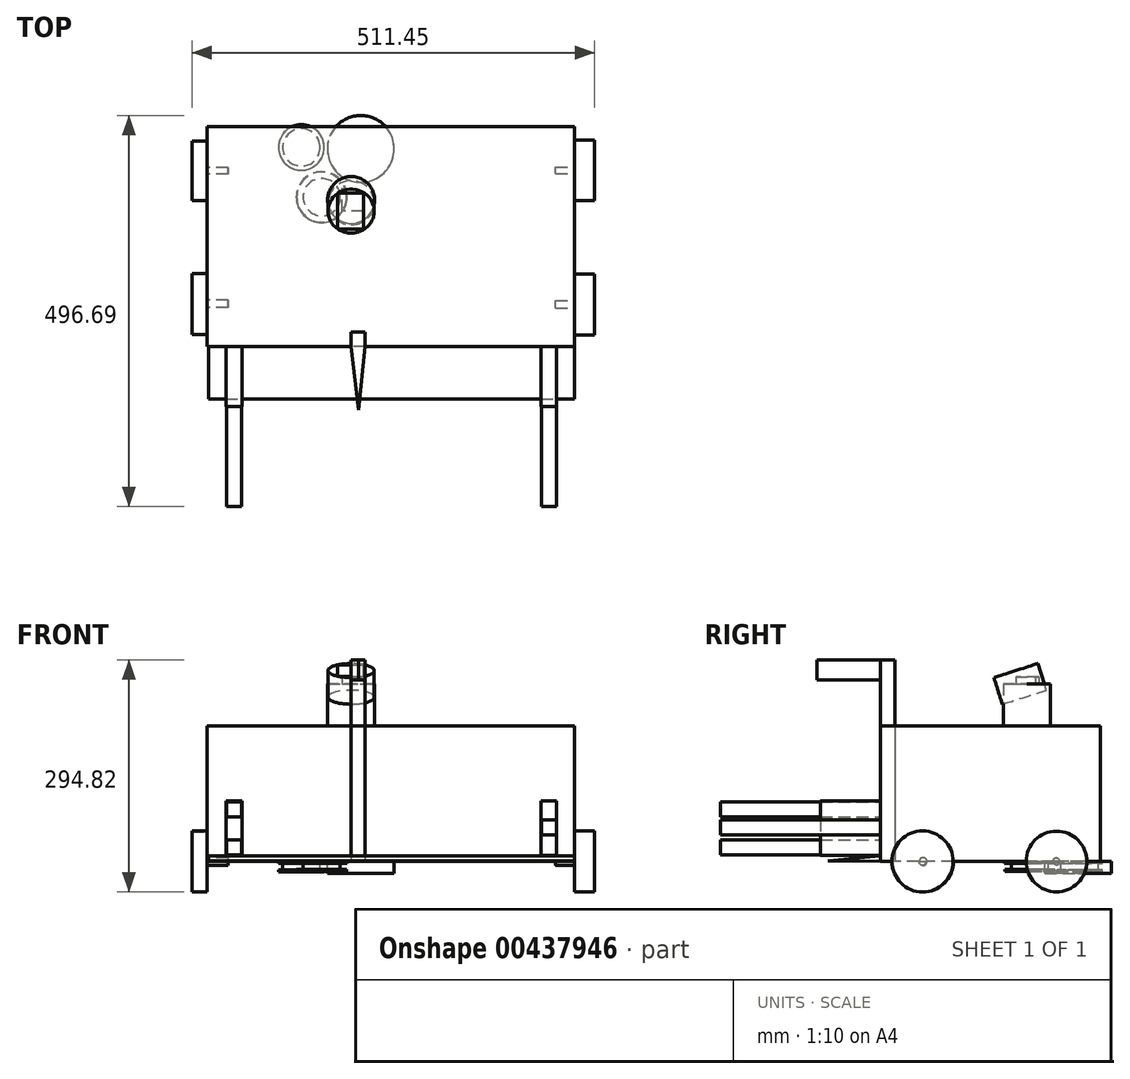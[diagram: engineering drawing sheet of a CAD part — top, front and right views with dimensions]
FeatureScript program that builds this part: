
annotation { "Feature Type Name" : "Feature", "Feature Type Description" : "" }
export const myFeature = defineFeature(function(context is Context, id is Id, definition is map)
    precondition{}
    {
        {
            var Q0;
            Q0=qCreatedBy(makeId("Front.planeOp"),FACE);
            var sketch = newSketch(context, id + "F0", { "sketchPlane" : qUnion([Q0])});
            skLineSegment(sketch, "E0.bottom", {"start": v(-158.36, 44.61) * mm, "end": v(-139.3, 44.61) * mm});
            skLineSegment(sketch, "E0.top", {"start": v(-158.36, 25.56) * mm, "end": v(-139.3, 25.56) * mm});
            skLineSegment(sketch, "E0.left", {"start": v(-158.36, 44.61) * mm, "end": v(-158.36, 25.56) * mm});
            skLineSegment(sketch, "E0.right", {"start": v(-139.3, 44.61) * mm, "end": v(-139.3, 25.56) * mm});
            skLineSegment(sketch, "E1.bottom", {"start": v(-158.13, -4.21) * mm, "end": v(-139.08, -4.21) * mm});
            skLineSegment(sketch, "E1.top", {"start": v(-158.13, -23.26) * mm, "end": v(-139.08, -23.26) * mm});
            skLineSegment(sketch, "E1.left", {"start": v(-158.13, -4.21) * mm, "end": v(-158.13, -23.26) * mm});
            skLineSegment(sketch, "E1.right", {"start": v(-139.08, -4.21) * mm, "end": v(-139.08, -23.26) * mm});
            skLineSegment(sketch, "E2.bottom", {"start": v(241.6, 21.7) * mm, "end": v(260.66, 21.7) * mm});
            skLineSegment(sketch, "E2.top", {"start": v(241.6, 2.65) * mm, "end": v(260.66, 2.65) * mm});
            skLineSegment(sketch, "E2.left", {"start": v(241.6, 21.7) * mm, "end": v(241.6, 2.65) * mm});
            skLineSegment(sketch, "E2.right", {"start": v(260.66, 21.7) * mm, "end": v(260.66, 2.65) * mm});
            skText(sketch, "E3", { "text": "carson anderson\n", "fontName": "OpenSans-Regular.ttf"});
            const initialGuessF0  = {"E3": [0.0572, 0.06518, 1, 0, 0.0084]};
            skSetInitialGuess(sketch, initialGuessF0);
            skSolve(sketch);
        }
        {
            var Q0;
            Q0=makeQuery(id+"F0.imprint","IMPRINT",FACE,{"disambiguationData":[TD([[makeQuery(id+"F0.imprint","IMPRINT",EDGE,{"derivedFrom":sQuery(id+"F0.wireOp",EDGE,"E0.bottom")}),-1.0]])]});
            var Q1;
            Q1=makeQuery(id+"F0.imprint","IMPRINT",FACE,{"disambiguationData":[TD([[makeQuery(id+"F0.imprint","IMPRINT",EDGE,{"derivedFrom":sQuery(id+"F0.wireOp",EDGE,"E1.bottom")}),-1.0]])]});
            var Q2;
            Q2=makeQuery(id+"F0.imprint","IMPRINT",FACE,{"disambiguationData":[TD([[makeQuery(id+"F0.imprint","IMPRINT",EDGE,{"derivedFrom":sQuery(id+"F0.wireOp",EDGE,"E2.bottom")}),-1.0]])]});
            extrude(context, id + "F1", {"entities" : qUnion([Q0, Q1, Q2]), "depth" : 203.2 * mm});
        }
        {
            var Q0;
            Q0=qCreatedBy(makeId("Front.planeOp"),FACE);
            var sketch = newSketch(context, id + "F2", { "sketchPlane" : qUnion([Q0])});
            skLineSegment(sketch, "E4.bottom", {"start": v(-138.56, 45.6) * mm, "end": v(-159.13, 45.6) * mm});
            skLineSegment(sketch, "E4.top", {"start": v(-138.56, -23.5) * mm, "end": v(-159.13, -23.5) * mm});
            skLineSegment(sketch, "E4.left", {"start": v(-138.56, 45.6) * mm, "end": v(-138.56, -23.5) * mm});
            skLineSegment(sketch, "E4.right", {"start": v(-159.13, 45.6) * mm, "end": v(-159.13, -23.5) * mm});
            skLineSegment(sketch, "E5.bottom", {"start": v(260.62, 45.42) * mm, "end": v(241.43, 45.42) * mm});
            skLineSegment(sketch, "E5.top", {"start": v(260.62, -23.5) * mm, "end": v(241.43, -23.5) * mm});
            skLineSegment(sketch, "E5.left", {"start": v(260.62, 45.42) * mm, "end": v(260.62, -23.5) * mm});
            skLineSegment(sketch, "E5.right", {"start": v(241.43, 45.42) * mm, "end": v(241.43, -23.5) * mm});
            skSolve(sketch);
        }
        {
            var Q0;
            Q0 = qSketchRegion(id + "F2", true);
            extrude(context, id + "F3", {"entities" : qUnion([Q0]), "depth" : 76.2 * mm});
        }
        {
            var Q0;
            Q0=qCreatedBy(makeId("Front.planeOp"),FACE);
            var sketch = newSketch(context, id + "F4", { "sketchPlane" : qUnion([Q0])});
            skLineSegment(sketch, "E6.bottom", {"start": v(283.8, -31.38) * mm, "end": v(-183.2, -31.38) * mm});
            skLineSegment(sketch, "E6.top", {"start": v(283.8, 140.95) * mm, "end": v(-183.2, 140.95) * mm});
            skLineSegment(sketch, "E6.left", {"start": v(283.8, -31.38) * mm, "end": v(283.8, 140.95) * mm});
            skLineSegment(sketch, "E6.right", {"start": v(-183.2, -31.38) * mm, "end": v(-183.2, 140.95) * mm});
            skSolve(sketch);
        }
        {
            var Q0;
            Q0 = qSketchRegion(id + "F4", true);
            extrude(context, id + "F5", {"entities" : qUnion([Q0]), "depth" : -279.4 * mm});
        }
        {
            var Q0;
            Q0=makeQuery(id+"F5.opExtrude","SWEPT_FACE",FACE,{"disambiguationData":[OSD([sQuery(id+"F4.wireOp",EDGE,"E6.right")])]});
            var sketch = newSketch(context, id + "F6", { "sketchPlane" : qUnion([Q0])});
            skCircle(sketch, "E7", {"center": v(-54.1, -31.38) * mm, "radius": 38.66 * mm});
            skCircle(sketch, "E8", {"center": v(-223.24, -31.38) * mm, "radius": 37.87 * mm});
            skSolve(sketch);
        }
        {
            var Q0;
            Q0 = qSketchRegion(id + "F6", true);
            extrude(context, id + "F7", {"entities" : qUnion([Q0]), "depth" : 19.05 * mm});
        }
        {
            var Q0;
            Q0=makeQuery(id+"F5.opExtrude","SWEPT_FACE",FACE,{"disambiguationData":[OSD([sQuery(id+"F4.wireOp",EDGE,"E6.right")])]});
            var sketch = newSketch(context, id + "F8", { "sketchPlane" : qUnion([Q0])});
            skCircle(sketch, "E9", {"center": v(-223.26, -31.38) * mm, "radius": 4.32 * mm});
            skCircle(sketch, "E10", {"center": v(-54.16, -31.38) * mm, "radius": 4.89 * mm});
            skSolve(sketch);
        }
        {
            var Q0;
            Q0 = qSketchRegion(id + "F8", true);
            extrude(context, id + "F9", {"entities" : qUnion([Q0]), "oppositeDirection" : true, "depth" : 26.92 * mm});
        }
        {
            var Q0;
            Q0=makeQuery(id+"F5.opExtrude","SWEPT_FACE",FACE,{"disambiguationData":[OSD([sQuery(id+"F4.wireOp",EDGE,"E6.left")])]});
            var sketch = newSketch(context, id + "F10", { "sketchPlane" : qUnion([Q0])});
            skCircle(sketch, "E11", {"center": v(53.46, -31.38) * mm, "radius": 38.79 * mm});
            skCircle(sketch, "E12", {"center": v(223.62, -31.38) * mm, "radius": 38.49 * mm});
            skSolve(sketch);
        }
        {
            var Q0;
            Q0 = qSketchRegion(id + "F10", true);
            extrude(context, id + "F11", {"entities" : qUnion([Q0]), "operationType" : NewBodyOperationType.ADD, "depth" : 25.4 * mm});
        }
        {
            var Q0;
            Q0=makeQuery(id+"F5.opExtrude","SWEPT_FACE",FACE,{"disambiguationData":[OSD([sQuery(id+"F4.wireOp",EDGE,"E6.left")])]});
            var sketch = newSketch(context, id + "F12", { "sketchPlane" : qUnion([Q0])});
            skCircle(sketch, "E13", {"center": v(53.46, -31.38) * mm, "radius": 4.7 * mm});
            skCircle(sketch, "E14", {"center": v(223.62, -31.38) * mm, "radius": 4.17 * mm});
            skSolve(sketch);
        }
        {
            var Q0;
            Q0 = qSketchRegion(id + "F12", true);
            extrude(context, id + "F13", {"entities" : qUnion([Q0]), "operationType" : NewBodyOperationType.ADD, "oppositeDirection" : true, "depth" : 24.13 * mm});
        }
        {
            var Q0;
            Q0=makeQuery(id+"F5.opExtrude","SWEPT_FACE",FACE,{"disambiguationData":[OSD([sQuery(id+"F4.wireOp",EDGE,"E6.left")])]});
            var sketch = newSketch(context, id + "F14", { "sketchPlane" : qUnion([Q0])});
            skLineSegment(sketch, "E15", {"start": v(0, -24.49) * mm, "end": v(-66.4, -30.82) * mm});
            skLineSegment(sketch, "E16", {"start": v(-66.4, -30.82) * mm, "end": v(0, -31.38) * mm});
            skLineSegment(sketch, "E17", {"start": v(0, -31.38) * mm, "end": v(0, -24.49) * mm});
            skSolve(sketch);
        }
        {
            var Q0;
            Q0 = qSketchRegion(id + "F14", true);
            var Q1;
            Q1=makeQuery(id+"FNswGk9dSfGoi4H_10.opExtrude","SWEPT_FACE",FACE,{"disambiguationData":[OSD([sQuery(id+"F14.wireOp",EDGE,"E15")])]});
            extrude(context, id + "F15", {"entities" : qUnion([Q0, Q1]), "oppositeDirection" : true, "depth" : 464.82 * mm});
        }
        {
            var Q0;
            Q0=makeQuery(id+"F5.opExtrude","SWEPT_FACE",FACE,{"disambiguationData":[OSD([sQuery(id+"F4.wireOp",EDGE,"E6.bottom")])]});
            var sketch = newSketch(context, id + "F16", { "sketchPlane" : qUnion([Q0])});
            skLineSegment(sketch, "E18.bottom", {"start": v(17.9, 0) * mm, "end": v(0, 0) * mm});
            skLineSegment(sketch, "E18.top", {"start": v(17.9, -18.49) * mm, "end": v(0, -18.49) * mm});
            skLineSegment(sketch, "E18.left", {"start": v(17.9, 0) * mm, "end": v(17.9, -18.49) * mm});
            skLineSegment(sketch, "E18.right", {"start": v(0, 0) * mm, "end": v(0, -18.49) * mm});
            skSolve(sketch);
        }
        {
            var Q0;
            Q0 = qSketchRegion(id + "F16", true);
            extrude(context, id + "F17", {"entities" : qUnion([Q0]), "oppositeDirection" : true, "depth" : 230.63 * mm});
        }
        {
            var Q0;
            Q0=makeQuery(id+"F17.opExtrude","CAP_FACE",FACE,{"disambiguationData":[OSD([sQuery(id+"F16.wireOp",EDGE,"E18.bottom"),sQuery(id+"F16.wireOp",EDGE,"E18.top"),sQuery(id+"F16.wireOp",EDGE,"E18.left"),sQuery(id+"F16.wireOp",EDGE,"E18.right")])],"isStart":false});
            var sketch = newSketch(context, id + "F18", { "sketchPlane" : qUnion([Q0])});
            skLineSegment(sketch, "E19", {"start": v(0, 18.49) * mm, "end": v(17.9, 18.49) * mm});
            skLineSegment(sketch, "E20", {"start": v(17.9, 18.49) * mm, "end": v(17.9, 0) * mm});
            skLineSegment(sketch, "E21", {"start": v(17.9, 0) * mm, "end": v(9.63, -80.6) * mm});
            skLineSegment(sketch, "E22", {"start": v(9.63, -80.6) * mm, "end": v(0, 0) * mm});
            skLineSegment(sketch, "E23", {"start": v(0, 0) * mm, "end": v(0, 18.49) * mm});
            skSolve(sketch);
        }
        {
            var Q0;
            Q0 = qSketchRegion(id + "F18", true);
            extrude(context, id + "F19", {"entities" : qUnion([Q0]), "operationType" : NewBodyOperationType.ADD, "depth" : 25.4 * mm});
        }
        {
            var Q0;
            Q0=makeQuery(id+"F5.opExtrude","SWEPT_FACE",FACE,{"disambiguationData":[OSD([sQuery(id+"F4.wireOp",EDGE,"E6.top")])]});
            var sketch = newSketch(context, id + "F20", { "sketchPlane" : qUnion([Q0])});
            skCircle(sketch, "E24", {"center": v(0, 186.04) * mm, "radius": 29.82 * mm});
            skSolve(sketch);
        }
        {
            var Q0;
            Q0 = qSketchRegion(id + "F20", true);
            extrude(context, id + "F21", {"entities" : qUnion([Q0]), "operationType" : NewBodyOperationType.ADD, "depth" : 53.34 * mm});
        }
        {
            var Q0;
            Q0=makeQuery(id+"F5.opExtrude","SWEPT_FACE",FACE,{"disambiguationData":[OSD([sQuery(id+"F4.wireOp",EDGE,"E6.top")])]});
            var sketch = newSketch(context, id + "F22", { "sketchPlane" : qUnion([Q0])});
            skLineSegment(sketch, "E25", {"start": v(-11.63, 201.1) * mm, "end": v(-11.63, 171.87) * mm});
            skLineSegment(sketch, "E26", {"start": v(-11.63, 171.87) * mm, "end": v(15.83, 171.87) * mm});
            skLineSegment(sketch, "E27", {"start": v(15.83, 171.87) * mm, "end": v(15.83, 196.67) * mm});
            skLineSegment(sketch, "E28", {"start": v(15.83, 196.67) * mm, "end": v(-11.63, 201.1) * mm});
            skSolve(sketch);
        }
        {
            var Q0;
            Q0 = qSketchRegion(id + "F22", true);
            extrude(context, id + "F23", {"entities" : qUnion([Q0]), "operationType" : NewBodyOperationType.ADD, "depth" : 61.98 * mm});
        }
        {
            var Q0;
            Q0=makeQuery(id+"F23.opExtrude","SWEPT_FACE",FACE,{"disambiguationData":[OSD([sQuery(id+"F22.wireOp",EDGE,"E27")])]});
            var sketch = newSketch(context, id + "F24", { "sketchPlane" : qUnion([Q0])});
            skLineSegment(sketch, "E29", {"start": v(149.38, 204) * mm, "end": v(194.67, 218.36) * mm});
            skLineSegment(sketch, "E30", {"start": v(194.67, 218.36) * mm, "end": v(149.38, 203.95) * mm});
            skLineSegment(sketch, "E31", {"start": v(149.38, 203.95) * mm, "end": v(149.38, 204) * mm});
            skSolve(sketch);
        }
        {
            var Q0;
            Q0 = qSketchRegion(id + "F24", true);
            extrude(context, id + "F25", {"entities" : qUnion([Q0]), "oppositeDirection" : true, "depth" : 33.02 * mm});
        }
        {
            var Q0;
            Q0=makeQuery(id+"F25.opExtrude","SWEPT_FACE",FACE,{"disambiguationData":[OSD([sQuery(id+"F24.wireOp",EDGE,"E29")])]});
            var sketch = newSketch(context, id + "F26", { "sketchPlane" : qUnion([Q0])});
            skCircle(sketch, "E32", {"center": v(0, 227.8) * mm, "radius": 29.32 * mm});
            skPoint(sketch, "E32.centerSnap0", {"position": v(-17.2, 227.8) * mm});
            skSolve(sketch);
        }
        {
            var Q0;
            Q0 = qSketchRegion(id + "F26", true);
            extrude(context, id + "F27", {"entities" : qUnion([Q0]), "oppositeDirection" : true, "depth" : 35.56 * mm});
        }
        {
            var Q0;
            Q0=makeQuery(id+"F5.opExtrude","SWEPT_FACE",FACE,{"disambiguationData":[OSD([sQuery(id+"F4.wireOp",EDGE,"E6.bottom")])]});
            var sketch = newSketch(context, id + "F28", { "sketchPlane" : qUnion([Q0])});
            skCircle(sketch, "E33", {"center": v(-63.17, -252.92) * mm, "radius": 29.02 * mm});
            skSolve(sketch);
        }
        {
            var Q0;
            Q0 = qSketchRegion(id + "F28", true);
            extrude(context, id + "F29", {"entities" : qUnion([Q0]), "operationType" : NewBodyOperationType.ADD, "depth" : 2.54 * mm});
        }
        {
            var Q0;
            Q0=makeQuery(id+"F29.opExtrude","CAP_FACE",FACE,{"disambiguationData":[OSD([sQuery(id+"F28.wireOp",EDGE,"E33")])],"isStart":false});
            var sketch = newSketch(context, id + "F30", { "sketchPlane" : qUnion([Q0])});
            skCircle(sketch, "E34", {"center": v(-63.17, -252.92) * mm, "radius": 23.76 * mm});
            skSolve(sketch);
        }
        {
            var Q0;
            Q0 = qSketchRegion(id + "F30", true);
            extrude(context, id + "F31", {"entities" : qUnion([Q0]), "operationType" : NewBodyOperationType.ADD, "depth" : 7.87 * mm});
        }
        {
            var Q0;
            Q0=makeQuery(id+"F31.opExtrude","CAP_FACE",FACE,{"disambiguationData":[OSD([sQuery(id+"F30.wireOp",EDGE,"E34")])],"isStart":false});
            var sketch = newSketch(context, id + "F32", { "sketchPlane" : qUnion([Q0])});
            skCircle(sketch, "E35", {"center": v(-63.17, -252.92) * mm, "radius": 28.9 * mm});
            skSolve(sketch);
        }
        {
            var Q0;
            Q0 = qSketchRegion(id + "F32", true);
            extrude(context, id + "F33", {"entities" : qUnion([Q0]), "operationType" : NewBodyOperationType.ADD, "depth" : 2.54 * mm});
        }
        {
            var Q0;
            Q0=makeQuery(id+"F5.opExtrude","SWEPT_FACE",FACE,{"disambiguationData":[OSD([sQuery(id+"F4.wireOp",EDGE,"E6.bottom")])]});
            var sketch = newSketch(context, id + "F34", { "sketchPlane" : qUnion([Q0])});
            skCircle(sketch, "E36", {"center": v(12.25, -251.1) * mm, "radius": 42.4 * mm});
            skSolve(sketch);
        }
        {
            var Q0;
            Q0 = qSketchRegion(id + "F34", true);
            extrude(context, id + "F35", {"entities" : qUnion([Q0]), "operationType" : NewBodyOperationType.ADD, "depth" : 15.24 * mm});
        }
        {
            var Q0;
            Q0=makeQuery(id+"F5.opExtrude","SWEPT_FACE",FACE,{"disambiguationData":[OSD([sQuery(id+"F4.wireOp",EDGE,"E6.bottom")])]});
            var sketch = newSketch(context, id + "F36", { "sketchPlane" : qUnion([Q0])});
            skCircle(sketch, "E37", {"center": v(-37.43, -189.77) * mm, "radius": 32.26 * mm});
            skSolve(sketch);
        }
        {
            var Q0;
            Q0 = qSketchRegion(id + "F36", true);
            extrude(context, id + "F37", {"entities" : qUnion([Q0]), "operationType" : NewBodyOperationType.ADD, "depth" : 2.54 * mm});
        }
        {
            var Q0;
            Q0=makeQuery(id+"F37.opExtrude","CAP_FACE",FACE,{"disambiguationData":[OSD([sQuery(id+"F36.wireOp",EDGE,"E37")])],"isStart":false});
            var sketch = newSketch(context, id + "F38", { "sketchPlane" : qUnion([Q0])});
            skCircle(sketch, "E38", {"center": v(-37.43, -189.77) * mm, "radius": 23.65 * mm});
            skSolve(sketch);
        }
        {
            var Q0;
            Q0 = qSketchRegion(id + "F38", true);
            extrude(context, id + "F39", {"entities" : qUnion([Q0]), "operationType" : NewBodyOperationType.ADD, "depth" : 7.62 * mm});
        }
        {
            var Q0;
            Q0=makeQuery(id+"F39.opExtrude","CAP_FACE",FACE,{"disambiguationData":[OSD([sQuery(id+"F38.wireOp",EDGE,"E38")])],"isStart":false});
            var sketch = newSketch(context, id + "F40", { "sketchPlane" : qUnion([Q0])});
            skCircle(sketch, "E39", {"center": v(-37.43, -189.77) * mm, "radius": 31.73 * mm});
            skSolve(sketch);
        }
        {
            var Q0;
            Q0 = qSketchRegion(id + "F40", true);
            extrude(context, id + "F41", {"entities" : qUnion([Q0]), "operationType" : NewBodyOperationType.ADD, "depth" : 2.54 * mm});
        }
    });
